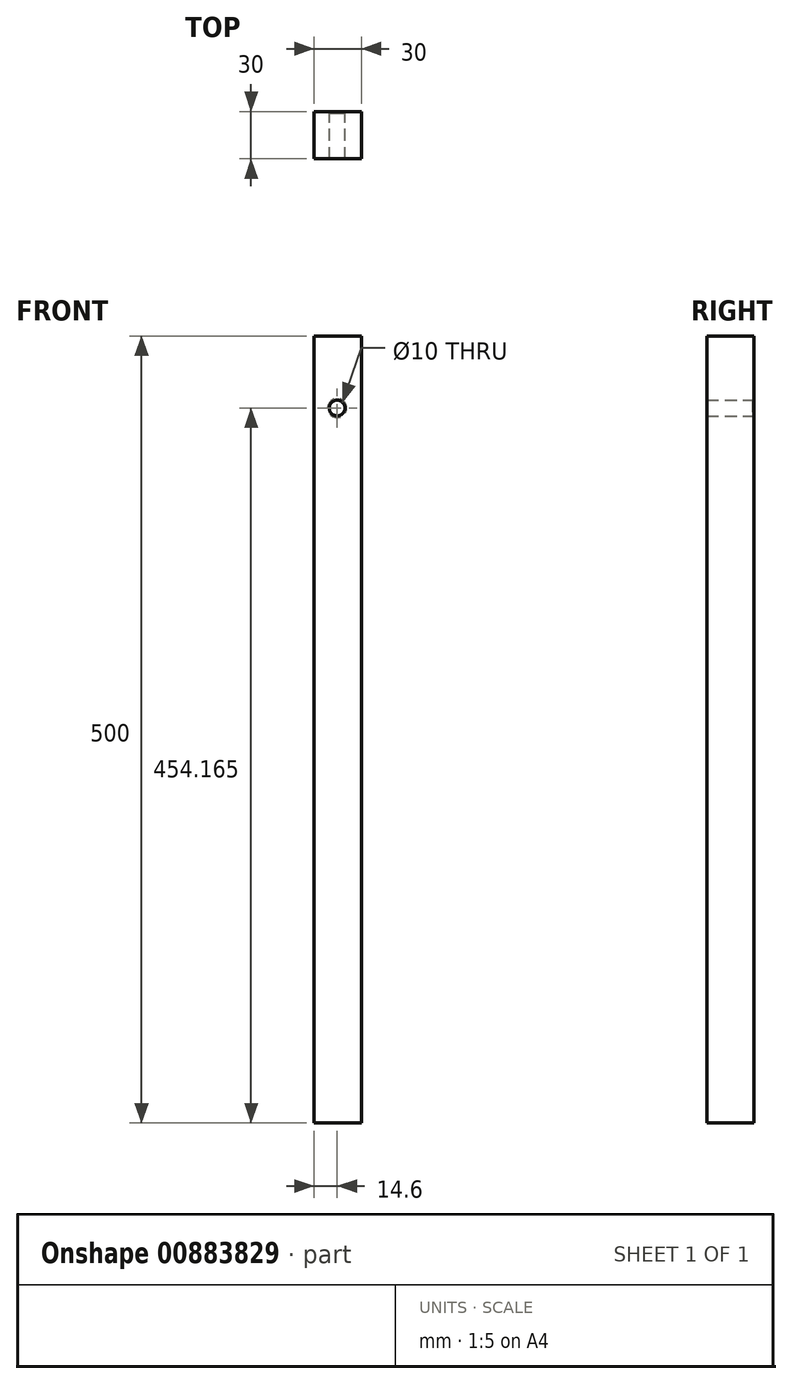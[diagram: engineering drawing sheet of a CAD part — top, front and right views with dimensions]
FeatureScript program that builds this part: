
annotation { "Feature Type Name" : "Feature", "Feature Type Description" : "" }
export const myFeature = defineFeature(function(context is Context, id is Id, definition is map)
    precondition{}
    {
        {
            var Q0;
            Q0=qCreatedBy(makeId("Front.planeOp"),FACE);
            var sketch = newSketch(context, id + "F0", { "sketchPlane" : qUnion([Q0])});
            skLineSegment(sketch, "E0.bottom", {"start": v(-14.6, 407.86) * mm, "end": v(15.4, 407.86) * mm});
            skLineSegment(sketch, "E0.top", {"start": v(-14.6, -92.14) * mm, "end": v(15.4, -92.14) * mm});
            skLineSegment(sketch, "E0.left", {"start": v(-14.6, 407.86) * mm, "end": v(-14.6, -92.14) * mm});
            skLineSegment(sketch, "E0.right", {"start": v(15.4, 407.86) * mm, "end": v(15.4, -92.14) * mm});
            skPoint(sketch, "E1", {"position": v(0, 362.03) * mm});
            skSolve(sketch);
        }
        {
            var Q0;
            Q0=makeQuery(id+"F0.imprint","IMPRINT",FACE,{"disambiguationData":[TD([[makeQuery(id+"F0.imprint","IMPRINT",EDGE,{"derivedFrom":sQuery(id+"F0.wireOp",EDGE,"E0.bottom")}),-1.0]])]});
            extrude(context, id + "F1", {"entities" : qUnion([Q0]), "depth" : 30 * mm, "offsetDistance" : 25 * mm});
        }
        {
            var Q0;
            Q0=sQuery(id+"F0.wireOp",VERTEX,"E1");
            var Q1;
            Q1=makeQuery(id+"F1.opExtrude","SWEPT_BODY",BODY,{"disambiguationData":[OSD([sQuery(id+"F0.wireOp",EDGE,"E0.bottom"),sQuery(id+"F0.wireOp",EDGE,"E0.top"),sQuery(id+"F0.wireOp",EDGE,"E0.left"),sQuery(id+"F0.wireOp",EDGE,"E0.right")])]});
            hole(context, id + "F2", {"style" : HoleStyle.C_SINK, "endStyle" : HoleEndStyle.THROUGH, "oppositeDirection" : true, "holeDiameter" : 10 * mm, "cSinkDiameter" : 12 * mm, "cSinkAngle" : 90 * degree, "majorDiameter" : 5 * mm, "isTappedThrough" : true, "tappedDepth" : 12 * mm, "tapClearance" : 3, "startFromSketch" : true, "locations" : qUnion([Q0]), "scope" : qUnion([Q1])});
        }
    });
